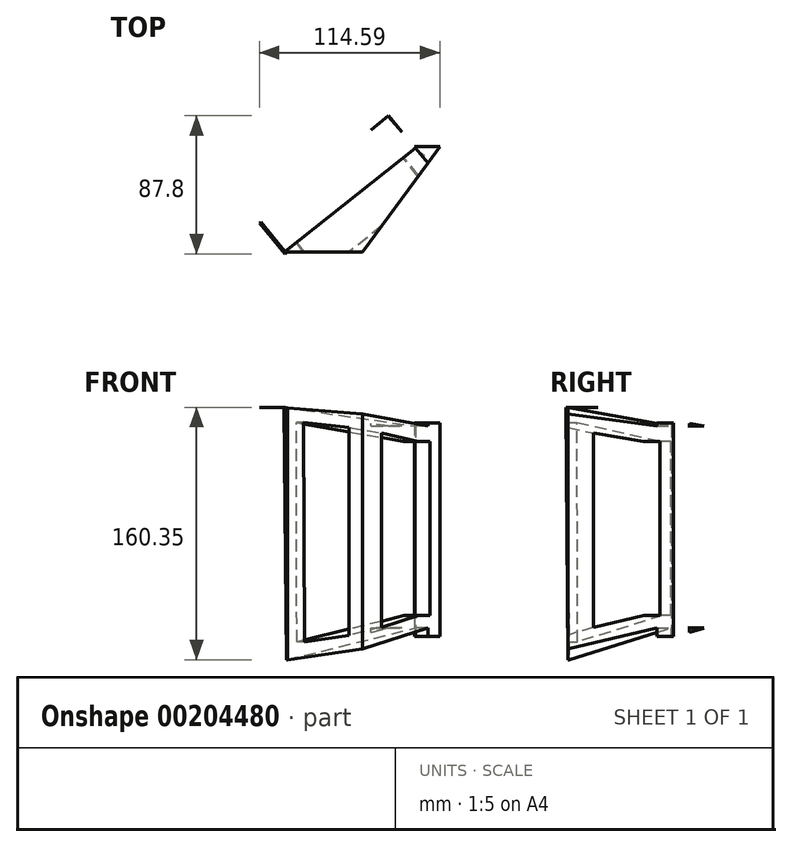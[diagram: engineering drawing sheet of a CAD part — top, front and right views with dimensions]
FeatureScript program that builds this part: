
annotation { "Feature Type Name" : "Feature", "Feature Type Description" : "" }
export const myFeature = defineFeature(function(context is Context, id is Id, definition is map)
    precondition{}
    {
        {
            var Q0;
            Q0=qCreatedBy(makeId("Top.planeOp"),FACE);
            var sketch = newSketch(context, id + "F0", { "sketchPlane" : qUnion([Q0])});
            skLineSegment(sketch, "E0", {"start": v(-18.27, 0) * mm, "end": v(10.07, 0) * mm});
            skLineSegment(sketch, "E1", {"start": v(10.07, 0) * mm, "end": v(59.07, 67.04) * mm});
            skLineSegment(sketch, "E2", {"start": v(59.07, 67.04) * mm, "end": v(42.65, 67.04) * mm});
            skLineSegment(sketch, "E3", {"start": v(42.65, 67.04) * mm, "end": v(-37.76, 0) * mm});
            skLineSegment(sketch, "E4", {"start": v(-37.76, 0) * mm, "end": v(10.07, 0) * mm});
            skSolve(sketch);
        }
        {
            var Q0;
            Q0 = qSketchRegion(id + "F0", true);
            extrude(context, id + "F1", {"entities" : qUnion([Q0]), "depth" : 76.51 * mm});
        }
        {
            var Q0;
            Q0=makeQuery(id+"F1.opExtrude","CAP_FACE",FACE,{"disambiguationData":[OSD([sQuery(id+"F0.wireOp",EDGE,"E1"),sQuery(id+"F0.wireOp",EDGE,"E2"),sQuery(id+"F0.wireOp",EDGE,"E3"),sQuery(id+"F0.wireOp",EDGE,"E4")])],"isStart":true});
            extrude(context, id + "F12", {"entities" : qUnion([Q0]), "operationType" : NewBodyOperationType.ADD, "depth" : 73.03 * mm});
        }
        {
            var Q0;
            Q0=makeQuery(id+"F12.opExtrude","CAP_FACE",FACE,{"disambiguationData":[OSD([sQuery(id+"F0.wireOp",EDGE,"E1"),sQuery(id+"F0.wireOp",EDGE,"E2"),sQuery(id+"F0.wireOp",EDGE,"E3"),sQuery(id+"F0.wireOp",EDGE,"E4")])],"isStart":false});
            extrude(context, id + "F2", {"entities" : qUnion([Q0]), "operationType" : NewBodyOperationType.ADD, "depth" : 14.27 * mm});
        }
        {
            var Q0;
            {var subQ0=sQuery(id+"F0.wireOp",EDGE,"E3");Q0=makeQuery(id+"F2.boolean.opBoolean","MERGE",FACE,{"derivedFrom":[makeQuery(id+"F12.boolean.opBoolean","MERGE",FACE,{"derivedFrom":[makeQuery(id+"F1.opExtrude","SWEPT_FACE",FACE,{"disambiguationData":[OSD([subQ0])]}),makeQuery(id+"F12.opExtrude","SWEPT_FACE",FACE,{"disambiguationData":[OSD([subQ0])]})]}),makeQuery(id+"F2.opExtrude","SWEPT_FACE",FACE,{"disambiguationData":[OSD([subQ0])]})]});}
            var sketch = newSketch(context, id + "F13", { "sketchPlane" : qUnion([Q0])});
            skLineSegment(sketch, "E5", {"start": v(29, -87.3) * mm, "end": v(-75.69, -67.15) * mm});
            skLineSegment(sketch, "E6", {"start": v(-75.69, -67.15) * mm, "end": v(-75.69, 61.2) * mm});
            skLineSegment(sketch, "E7", {"start": v(-75.69, 61.2) * mm, "end": v(30.95, 73.04) * mm});
            skLineSegment(sketch, "E8", {"start": v(30.95, 73.04) * mm, "end": v(29, -87.3) * mm});
            skSolve(sketch);
        }
        {
            var Q0;
            Q0 = qSketchRegion(id + "F13", true);
            extrude(context, id + "F3", {"entities" : qUnion([Q0]), "operationType" : NewBodyOperationType.ADD, "depth" : 25.4 * mm});
        }
        {
            var Q0;
            {var subQ2=sQuery(id+"F13.wireOp",EDGE,"E7");var subQ3=sQuery(id+"F0.wireOp",EDGE,"E3");Q0=makeQuery(id+"F3.boolean.opBoolean","SPLIT",FACE,{"disambiguationData":[TD([makeQuery(id+"F3.opExtrude","SWEPT_FACE",FACE,{"disambiguationData":[OSD([subQ2])]})])],"derivedFrom":makeQuery(id+"F2.boolean.opBoolean","MERGE",FACE,{"derivedFrom":[makeQuery(id+"F12.boolean.opBoolean","MERGE",FACE,{"derivedFrom":[makeQuery(id+"F1.opExtrude","SWEPT_FACE",FACE,{"disambiguationData":[OSD([subQ3])]}),makeQuery(id+"F12.opExtrude","SWEPT_FACE",FACE,{"disambiguationData":[OSD([subQ3])]})]}),makeQuery(id+"F2.opExtrude","SWEPT_FACE",FACE,{"disambiguationData":[OSD([subQ3])]})]})});}
            extrude(context, id + "F4", {"entities" : qUnion([Q0]), "operationType" : NewBodyOperationType.REMOVE, "oppositeDirection" : true, "depth" : 61.84 * mm});
        }
        {
            var Q0;
            {var subQ2=sQuery(id+"F13.wireOp",EDGE,"E5");var subQ4=sQuery(id+"F0.wireOp",EDGE,"E3");Q0=makeQuery(id+"F3.boolean.opBoolean","SPLIT",FACE,{"disambiguationData":[TD([makeQuery(id+"F3.opExtrude","SWEPT_FACE",FACE,{"disambiguationData":[OSD([subQ2])]})])],"derivedFrom":makeQuery(id+"F2.boolean.opBoolean","MERGE",FACE,{"derivedFrom":[makeQuery(id+"F12.boolean.opBoolean","MERGE",FACE,{"derivedFrom":[makeQuery(id+"F1.opExtrude","SWEPT_FACE",FACE,{"disambiguationData":[OSD([subQ4])]}),makeQuery(id+"F12.opExtrude","SWEPT_FACE",FACE,{"disambiguationData":[OSD([subQ4])]})]}),makeQuery(id+"F2.opExtrude","SWEPT_FACE",FACE,{"disambiguationData":[OSD([subQ4])]})]})});}
            extrude(context, id + "F14", {"entities" : qUnion([Q0]), "operationType" : NewBodyOperationType.REMOVE, "oppositeDirection" : true, "depth" : 90.7 * mm});
        }
        {
            var Q0;
            Q0=qCreatedBy(makeId("Top.planeOp"),FACE);
            var sketch = newSketch(context, id + "F5", { "sketchPlane" : qUnion([Q0])});
            skLineSegment(sketch, "E9", {"start": v(43.94, 66.11) * mm, "end": v(-39.52, 0) * mm});
            skLineSegment(sketch, "E10", {"start": v(-39.52, 0) * mm, "end": v(-55.13, 19.71) * mm});
            skLineSegment(sketch, "E11", {"start": v(-55.13, 19.71) * mm, "end": v(26.17, 86.2) * mm});
            skLineSegment(sketch, "E12", {"start": v(26.17, 86.2) * mm, "end": v(43.94, 66.11) * mm});
            skSolve(sketch);
        }
        {
            var Q0;
            Q0 = qSketchRegion(id + "F5", true);
            extrude(context, id + "F15", {"entities" : qUnion([Q0]), "operationType" : NewBodyOperationType.REMOVE, "oppositeDirection" : true, "depth" : 131.9 * mm});
        }
        {
            var Q0;
            Q0=makeQuery(id+"F15.boolean.opBoolean","COPY",FACE,{"derivedFrom":makeQuery(id+"F15.opExtrude","CAP_FACE",FACE,{"disambiguationData":[OSD([sQuery(id+"F5.wireOp",EDGE,"E9"),sQuery(id+"F5.wireOp",EDGE,"E10"),sQuery(id+"F5.wireOp",EDGE,"E11"),sQuery(id+"F5.wireOp",EDGE,"E12")])],"isStart":true})});
            extrude(context, id + "F16", {"entities" : qUnion([Q0]), "operationType" : NewBodyOperationType.REMOVE, "oppositeDirection" : true, "depth" : 288.8 * mm});
        }
        {
            var Q0;
            Q0=makeQuery(id+"F3.opExtrude","SWEPT_FACE",FACE,{"disambiguationData":[OSD([sQuery(id+"F13.wireOp",EDGE,"E6")])]});
            extrude(context, id + "F17", {"entities" : qUnion([Q0]), "operationType" : NewBodyOperationType.REMOVE, "oppositeDirection" : true, "depth" : 203.67 * mm});
        }
        {
            var Q0;
            {var subQ0=sQuery(id+"F5.wireOp",EDGE,"E10");Q0=makeQuery(id+"F16.boolean.opBoolean","MERGE",FACE,{"derivedFrom":[makeQuery(id+"F15.boolean.opBoolean","COPY",FACE,{"derivedFrom":makeQuery(id+"F15.opExtrude","SWEPT_FACE",FACE,{"disambiguationData":[OSD([subQ0])]})}),makeQuery(id+"F16.opExtrude","SWEPT_FACE",FACE,{"disambiguationData":[OSD([subQ0])]})]});}
            var Q1;
            Q1=makeQuery(id+"F16.boolean.opBoolean","COPY",FACE,{"derivedFrom":makeQuery(id+"F16.opExtrude","SWEPT_FACE",FACE,{"disambiguationData":[OSD([sQuery(id+"F13.wireOp",EDGE,"E8"),sQuery(id+"F5.wireOp",EDGE,"E9"),sQuery(id+"F5.wireOp",EDGE,"E10"),sQuery(id+"F5.wireOp",EDGE,"E11"),sQuery(id+"F5.wireOp",EDGE,"E12")])]})});
            extrude(context, id + "F6", {"entities" : qUnion([Q0, Q1]), "operationType" : NewBodyOperationType.REMOVE, "oppositeDirection" : true, "depth" : 49.5 * mm});
        }
        {
            var Q0;
            {var subQ0=sQuery(id+"F0.wireOp",EDGE,"E2");Q0=makeQuery(id+"F2.boolean.opBoolean","MERGE",FACE,{"derivedFrom":[makeQuery(id+"F12.boolean.opBoolean","MERGE",FACE,{"derivedFrom":[makeQuery(id+"F1.opExtrude","SWEPT_FACE",FACE,{"disambiguationData":[OSD([subQ0])]}),makeQuery(id+"F12.opExtrude","SWEPT_FACE",FACE,{"disambiguationData":[OSD([subQ0])]})]}),makeQuery(id+"F2.opExtrude","SWEPT_FACE",FACE,{"disambiguationData":[OSD([subQ0])]})]});}
            var sketch = newSketch(context, id + "F18", { "sketchPlane" : qUnion([Q0])});
            skLineSegment(sketch, "E13.bottom", {"start": v(-43.12, 63.14) * mm, "end": v(-59.07, 63.14) * mm});
            skLineSegment(sketch, "E13.top", {"start": v(-43.12, 76.51) * mm, "end": v(-59.07, 76.51) * mm});
            skLineSegment(sketch, "E13.left", {"start": v(-43.12, 63.14) * mm, "end": v(-43.12, 76.51) * mm});
            skLineSegment(sketch, "E13.right", {"start": v(-59.07, 63.14) * mm, "end": v(-59.07, 76.51) * mm});
            skSolve(sketch);
        }
        {
            var Q0;
            Q0 = qSketchRegion(id + "F18", true);
            extrude(context, id + "F7", {"entities" : qUnion([Q0]), "operationType" : NewBodyOperationType.REMOVE, "oppositeDirection" : true, "depth" : 25.4 * mm});
        }
        {
            var Q0;
            {var subQ0=sQuery(id+"F0.wireOp",EDGE,"E2");Q0=makeQuery(id+"F2.boolean.opBoolean","MERGE",FACE,{"derivedFrom":[makeQuery(id+"F12.boolean.opBoolean","MERGE",FACE,{"derivedFrom":[makeQuery(id+"F1.opExtrude","SWEPT_FACE",FACE,{"disambiguationData":[OSD([subQ0])]}),makeQuery(id+"F12.opExtrude","SWEPT_FACE",FACE,{"disambiguationData":[OSD([subQ0])]})]}),makeQuery(id+"F2.opExtrude","SWEPT_FACE",FACE,{"disambiguationData":[OSD([subQ0])]})]});}
            extrude(context, id + "F19", {"entities" : qUnion([Q0]), "operationType" : NewBodyOperationType.ADD, "depth" : 25.4 * mm});
        }
        {
            var Q0;
            Q0=makeQuery(id+"F19.opExtrude","CAP_FACE",FACE,{"disambiguationData":[OSD([sQuery(id+"F0.wireOp",EDGE,"E2")])],"isStart":false});
            var sketch = newSketch(context, id + "F20", { "sketchPlane" : qUnion([Q0])});
            skLineSegment(sketch, "E14.bottom", {"start": v(-43.12, -72.5) * mm, "end": v(-59.07, -72.5) * mm});
            skLineSegment(sketch, "E14.top", {"start": v(-43.12, -87.3) * mm, "end": v(-59.07, -87.3) * mm});
            skLineSegment(sketch, "E14.left", {"start": v(-43.12, -72.5) * mm, "end": v(-43.12, -87.3) * mm});
            skLineSegment(sketch, "E14.right", {"start": v(-59.07, -72.5) * mm, "end": v(-59.07, -87.3) * mm});
            skSolve(sketch);
        }
        {
            var Q0;
            Q0 = qSketchRegion(id + "F20", true);
            extrude(context, id + "F8", {"entities" : qUnion([Q0]), "operationType" : NewBodyOperationType.REMOVE, "oppositeDirection" : true, "depth" : 79.17 * mm});
        }
        {
            var Q0;
            {var subQ0=sQuery(id+"F18.wireOp",EDGE,"E13.bottom");Q0=makeQuery(id+"F19.boolean.opBoolean","MERGE",FACE,{"derivedFrom":[makeQuery(id+"F7.boolean.opBoolean","COPY",FACE,{"derivedFrom":makeQuery(id+"F7.opExtrude","SWEPT_FACE",FACE,{"disambiguationData":[OSD([subQ0])]})}),makeQuery(id+"F19.opExtrude","SWEPT_FACE",FACE,{"disambiguationData":[OSD([subQ0])]})]});}
            var sketch = newSketch(context, id + "F21", { "sketchPlane" : qUnion([Q0])});
            skLineSegment(sketch, "E15.bottom", {"start": v(43.12, 92.44) * mm, "end": v(59.07, 92.44) * mm});
            skLineSegment(sketch, "E15.top", {"start": v(43.12, 67.04) * mm, "end": v(59.07, 67.04) * mm});
            skLineSegment(sketch, "E15.left", {"start": v(43.12, 92.44) * mm, "end": v(43.12, 67.04) * mm});
            skLineSegment(sketch, "E15.right", {"start": v(59.07, 92.44) * mm, "end": v(59.07, 67.04) * mm});
            skSolve(sketch);
        }
        {
            var Q0;
            Q0 = qSketchRegion(id + "F21", true);
            extrude(context, id + "F22", {"entities" : qUnion([Q0]), "operationType" : NewBodyOperationType.REMOVE, "oppositeDirection" : true, "depth" : 143.02 * mm});
        }
        {
            var Q0;
            {var subQ0=sQuery(id+"F5.wireOp",EDGE,"E12");var subQ1=sQuery(id+"F5.wireOp",EDGE,"E11");var subQ2=sQuery(id+"F5.wireOp",EDGE,"E10");var subQ3=sQuery(id+"F5.wireOp",EDGE,"E9");var subQ4=makeQuery(id+"F15.opExtrude","SWEPT_FACE",FACE,{"disambiguationData":[OSD([subQ3])]});var subQ5=sQuery(id+"F13.wireOp",EDGE,"E8");Q0=makeQuery(id+"F6.boolean.opBoolean","MERGE",FACE,{"derivedFrom":[makeQuery(id+"F16.boolean.opBoolean","MERGE",FACE,{"derivedFrom":[makeQuery(id+"F15.boolean.opBoolean","COPY",FACE,{"derivedFrom":subQ4}),makeQuery(id+"F16.opExtrude","SWEPT_FACE",FACE,{"disambiguationData":[OSD([subQ3])]})]}),makeQuery(id+"F6.opExtrude","SWEPT_FACE",FACE,{"disambiguationData":[OSD([subQ5,subQ3,subQ2,subQ1,subQ0]),TDD([makeQuery(id+"F16.boolean.opBoolean","COPY",EDGE,{"derivedFrom":makeQuery(id+"F16.opExtrude","SWEPT_EDGE",EDGE,{"disambiguationData":[OSD([subQ5,subQ3,subQ2,subQ1,subQ0]),TDD([makeQuery(id+"F15.boolean.opBoolean","INTERSECT",VERTEX,{"derivedFrom":[makeQuery(id+"F3.opExtrude","SWEPT_FACE",FACE,{"disambiguationData":[OSD([subQ5])]}),subQ4,makeQuery(id+"F15.opExtrude","CAP_FACE",FACE,{"disambiguationData":[OSD([subQ3,subQ2,subQ1,subQ0])],"isStart":true})]})])]})})])]})]});}
            var sketch = newSketch(context, id + "F23", { "sketchPlane" : qUnion([Q0])});
            skLineSegment(sketch, "E16", {"start": v(-65.8, -59.23) * mm, "end": v(21.05, -75.95) * mm});
            skLineSegment(sketch, "E17", {"start": v(21.05, -75.95) * mm, "end": v(21.45, 63.5) * mm});
            skLineSegment(sketch, "E18", {"start": v(21.45, 63.5) * mm, "end": v(-65.16, 51.45) * mm});
            skLineSegment(sketch, "E19", {"start": v(-65.16, 51.45) * mm, "end": v(-65.8, -59.23) * mm});
            skSolve(sketch);
        }
        {
            var Q0;
            Q0 = qSketchRegion(id + "F23", true);
            extrude(context, id + "F9", {"entities" : qUnion([Q0]), "operationType" : NewBodyOperationType.REMOVE, "oppositeDirection" : true, "depth" : 25.4 * mm});
        }
        {
            var Q0;
            {var subQ0=sQuery(id+"F0.wireOp",EDGE,"E1");Q0=makeQuery(id+"F2.boolean.opBoolean","MERGE",FACE,{"derivedFrom":[makeQuery(id+"F12.boolean.opBoolean","MERGE",FACE,{"derivedFrom":[makeQuery(id+"F1.opExtrude","SWEPT_FACE",FACE,{"disambiguationData":[OSD([subQ0])]}),makeQuery(id+"F12.opExtrude","SWEPT_FACE",FACE,{"disambiguationData":[OSD([subQ0])]})]}),makeQuery(id+"F2.opExtrude","SWEPT_FACE",FACE,{"disambiguationData":[OSD([subQ0])]})]});}
            var sketch = newSketch(context, id + "F10", { "sketchPlane" : qUnion([Q0])});
            skLineSegment(sketch, "E20.bottom", {"start": v(65.35, 51.45) * mm, "end": v(78.62, 51.45) * mm});
            skLineSegment(sketch, "E20.top", {"start": v(65.35, -59.17) * mm, "end": v(78.62, -59.17) * mm});
            skLineSegment(sketch, "E20.left", {"start": v(65.35, 51.45) * mm, "end": v(65.35, -59.17) * mm});
            skLineSegment(sketch, "E20.right", {"start": v(78.62, 51.45) * mm, "end": v(78.62, -59.17) * mm});
            skSolve(sketch);
        }
        {
            var Q0;
            Q0 = qSketchRegion(id + "F10", true);
            extrude(context, id + "F11", {"entities" : qUnion([Q0]), "operationType" : NewBodyOperationType.REMOVE, "oppositeDirection" : true, "depth" : 25.4 * mm});
        }
    });
